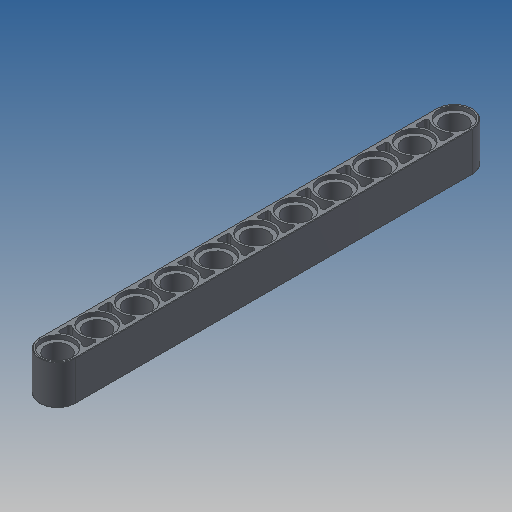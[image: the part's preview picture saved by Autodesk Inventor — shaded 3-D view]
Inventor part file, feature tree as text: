
AUTODESK INVENTOR PART (.ipt)
format: ipt  version: 2022.2 (Build 262287000, 287)  size: 447,488 bytes
history: native  units: mm
features: extrude x3, sketch x2, mirror x1, fillet x1
ambient origin geometry x8: Origin, YZ Plane, XZ Plane, XY Plane, X Axis, Y Axis, Z Axis, Center Point
bodies: Solid1 (feature_tree)
feature tree (7):
  extrude  "Extrusion1"  Depth=7.2mm
  sketch  "Sketch6"  dims[d41=0.8mm d42=0.0mm d43=3.1mm d44=0.0mm d48=80.0mm d49=6.4mm d50=4.8mm d51=8.0mm d52=0.8mm d53=100.0mm d55=8.0mm d56=10.0mm d58=10.0mm d60=0.4mm d61=0.1mm]
  extrude  "Extrusion7"  Depth=3.1mm TaperAngle=0.0deg
  extrude  "Extrusion8"  Depth=0.1mm
  mirror  "Mirror1"
  fillet  "Fillet2"  Radius=6.4mm
  sketch  "Sketch1"  dims[d14=8.0mm d15=0.0mm d32=7.2mm]
